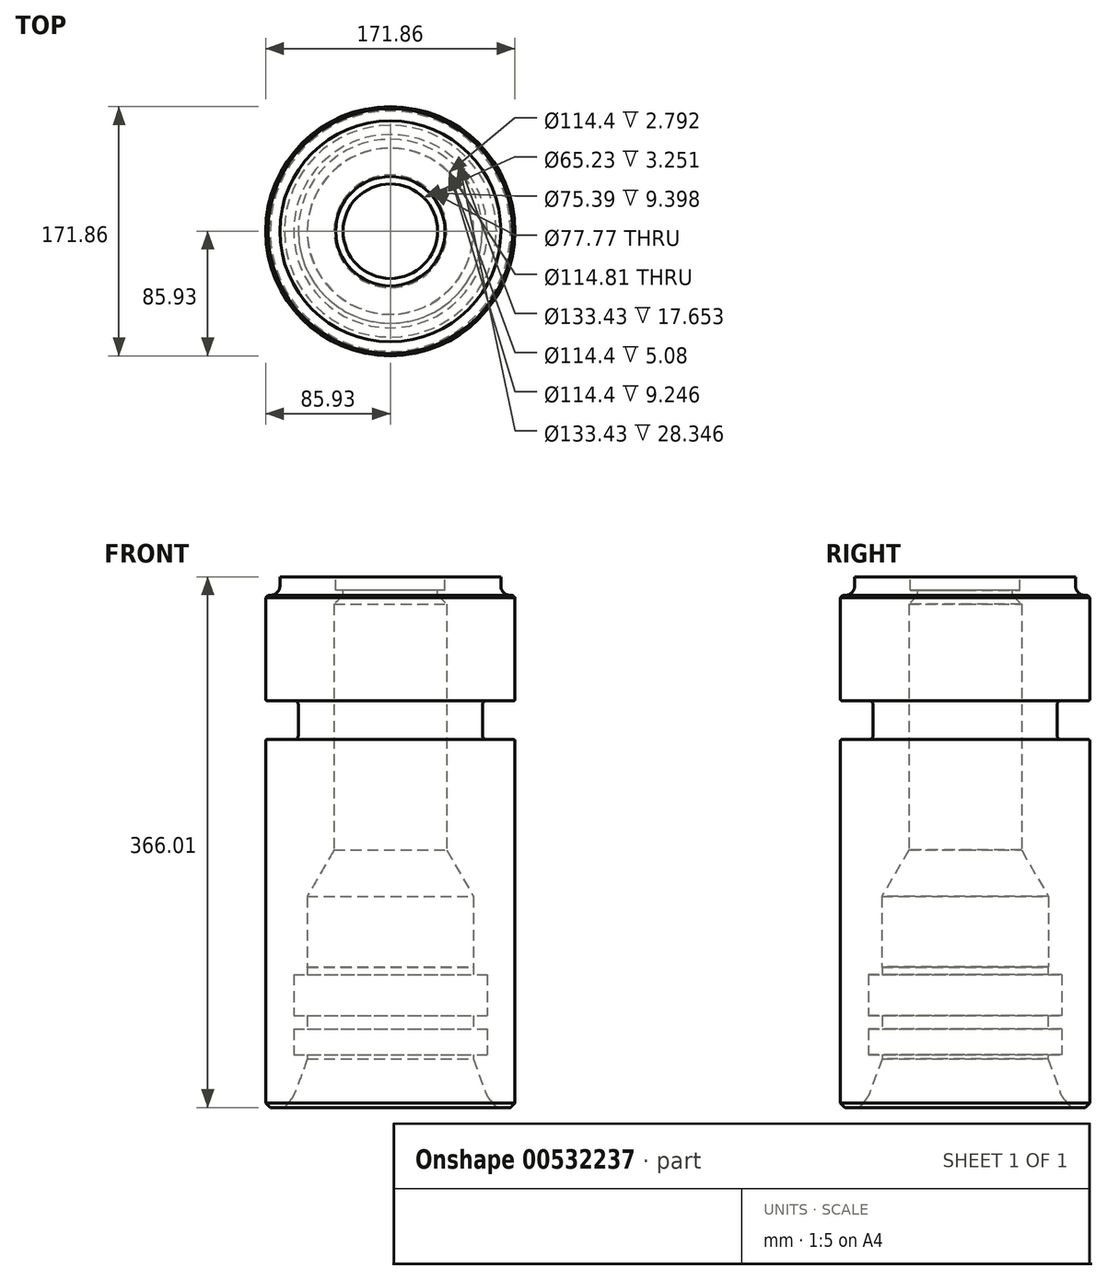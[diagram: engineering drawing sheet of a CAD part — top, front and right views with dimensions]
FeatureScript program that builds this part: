
annotation { "Feature Type Name" : "Feature", "Feature Type Description" : "" }
export const myFeature = defineFeature(function(context is Context, id is Id, definition is map)
    precondition{}
    {
        {
            var Q0;
            Q0=qCreatedBy(makeId("Front.planeOp"),FACE);
            var sketch = newSketch(context, id + "F0", { "sketchPlane" : qUnion([Q0])});
            skLineSegment(sketch, "E0", {"start": v(0, 0) * mm, "end": v(76.2, 0) * mm});
            skLineSegment(sketch, "E1", {"start": v(85.93, -12.7) * mm, "end": v(85.93, -85.34) * mm});
            skLineSegment(sketch, "E2", {"start": v(85.93, -366.01) * mm, "end": v(0, -366.01) * mm});
            skLineSegment(sketch, "E3", {"start": v(0, -366.01) * mm, "end": v(0, 0) * mm});
            skLineSegment(sketch, "E4", {"start": v(85.93, -112.27) * mm, "end": v(63.46, -112.27) * mm});
            skLineSegment(sketch, "E5", {"start": v(63.46, -112.27) * mm, "end": v(63.46, -85.34) * mm});
            skLineSegment(sketch, "E6", {"start": v(63.46, -85.34) * mm, "end": v(85.93, -85.34) * mm});
            skLineSegment(sketch, "E7.trimOffspring", {"start": v(85.93, -112.27) * mm, "end": v(85.93, -366.01) * mm});
            skLineSegment(sketch, "E8", {"start": v(85.93, -12.7) * mm, "end": v(76.2, -12.7) * mm});
            skLineSegment(sketch, "E9", {"start": v(76.2, -12.7) * mm, "end": v(76.2, 0) * mm});
            skPoint(sketch, "E10.orphan", {"position": v(85.93, 0) * mm});
            skSolve(sketch);
        }
        {
            var Q0;
            Q0=makeQuery(id+"F0.imprint","IMPRINT",FACE,{"disambiguationData":[TD([[makeQuery(id+"F0.imprint","IMPRINT",EDGE,{"derivedFrom":sQuery(id+"F0.wireOp",EDGE,"E0")}),-1.0]])]});
            var Q1;
            Q1=sQuery(id+"F0.wireOp",EDGE,"E3");
            revolve(context, id + "F1", {"entities" : qUnion([Q0]), "axis" : qUnion([Q1]), "revolveType" : RevolveType.FULL});
        }
        {
            var Q0;
            Q0=makeQuery(id+"F1.opRevolve","SWEPT_EDGE",EDGE,{"disambiguationData":[OSD([sQuery(id+"F0.wireOp",EDGE,"E8"),sQuery(id+"F0.wireOp",EDGE,"E9")])]});
            fillet(context, id + "F2", {"entities" : qUnion([Q0]), "radius" : 6.35 * mm, "tangentPropagation" : true, "allowEdgeOverflow" : false});
        }
        {
            var Q0;
            Q0=makeQuery(id+"F1.opRevolve","SWEPT_EDGE",EDGE,{"disambiguationData":[OSD([sQuery(id+"F0.wireOp",EDGE,"E1"),sQuery(id+"F0.wireOp",EDGE,"E8")])]});
            chamfer(context, id + "F3", {"entities" : qUnion([Q0]), "chamferType" : ChamferType.OFFSET_ANGLE, "width" : 1.52 * mm, "oppositeDirection" : false, "angle" : 45 * degree, "tangentPropagation" : true});
        }
        {
            var Q0;
            Q0=makeQuery(id+"F1.opRevolve","SWEPT_FACE",FACE,{"disambiguationData":[OSD([sQuery(id+"F0.wireOp",EDGE,"E0")])]});
            var sketch = newSketch(context, id + "F4", { "sketchPlane" : qUnion([Q0])});
            skCircle(sketch, "E11", {"center": v(0, 0) * mm, "radius": 32.61 * mm});
            skSolve(sketch);
        }
        {
            var Q0;
            Q0=makeQuery(id+"F4.imprint","IMPRINT",FACE,{"disambiguationData":[TD([[makeQuery(id+"F4.imprint","IMPRINT",EDGE,{"derivedFrom":sQuery(id+"F4.wireOp",EDGE,"E11")}),1.0]])]});
            var Q1;
            Q1=sQuery(id+"F4.wireOp",EDGE,"E11");
            extrude(context, id + "F5", {"entities" : qUnion([Q0]), "operationType" : NewBodyOperationType.REMOVE, "surfaceEntities" : qUnion([Q1]), "endBound" : BoundingType.THROUGH_ALL, "oppositeDirection" : true, "depth" : 25.4 * mm, "offsetDistance" : 25.4 * mm});
        }
        {
            var Q0;
            Q0=makeQuery(id+"F1.opRevolve","SWEPT_FACE",FACE,{"disambiguationData":[OSD([sQuery(id+"F0.wireOp",EDGE,"E2")])]});
            var sketch = newSketch(context, id + "F6", { "sketchPlane" : qUnion([Q0])});
            skCircle(sketch, "E12", {"center": v(0, 0) * mm, "radius": 57.2 * mm});
            skSolve(sketch);
        }
        {
            var Q0;
            Q0=makeQuery(id+"F6.imprint","IMPRINT",FACE,{"disambiguationData":[TD([[makeQuery(id+"F6.imprint","IMPRINT",EDGE,{"derivedFrom":sQuery(id+"F6.wireOp",EDGE,"E12")}),1.0]])]});
            var Q1;
            Q1=sQuery(id+"F6.wireOp",EDGE,"E12");
            extrude(context, id + "F7", {"entities" : qUnion([Q0]), "operationType" : NewBodyOperationType.REMOVE, "surfaceEntities" : qUnion([Q1]), "oppositeDirection" : true, "depth" : 145.54 * mm, "offsetDistance" : 25.4 * mm});
        }
        {
            var Q0;
            Q0=makeQuery(id+"F1.opRevolve","SWEPT_FACE",FACE,{"disambiguationData":[OSD([sQuery(id+"F0.wireOp",EDGE,"E0")])]});
            var sketch = newSketch(context, id + "F8", { "sketchPlane" : qUnion([Q0])});
            skCircle(sketch, "E13", {"center": v(0, 0) * mm, "radius": 37.7 * mm});
            skSolve(sketch);
        }
        {
            var Q0;
            Q0=makeQuery(id+"F8.imprint","IMPRINT",FACE,{"disambiguationData":[TD([[makeQuery(id+"F8.imprint","IMPRINT",EDGE,{"derivedFrom":sQuery(id+"F8.wireOp",EDGE,"E13")}),1.0]])]});
            var Q1;
            Q1=sQuery(id+"F8.wireOp",EDGE,"E13");
            extrude(context, id + "F9", {"entities" : qUnion([Q0]), "operationType" : NewBodyOperationType.REMOVE, "surfaceEntities" : qUnion([Q1]), "oppositeDirection" : true, "depth" : 9.4 * mm, "offsetDistance" : 25.4 * mm});
        }
        {
            var Q0;
            Q0=makeQuery(id+"F1.opRevolve","SWEPT_FACE",FACE,{"disambiguationData":[OSD([sQuery(id+"F0.wireOp",EDGE,"E2")])]});
            var sketch = newSketch(context, id + "F10", { "sketchPlane" : qUnion([Q0])});
            skCircle(sketch, "E14", {"center": v(0, 0) * mm, "radius": 38.89 * mm});
            skSolve(sketch);
        }
        {
            var Q0;
            Q0=makeQuery(id+"F10.imprint","IMPRINT",FACE,{"disambiguationData":[TD([[makeQuery(id+"F10.imprint","IMPRINT",EDGE,{"derivedFrom":sQuery(id+"F10.wireOp",EDGE,"E14")}),1.0]])]});
            var Q1;
            Q1=sQuery(id+"F10.wireOp",EDGE,"E14");
            extrude(context, id + "F11", {"entities" : qUnion([Q0]), "operationType" : NewBodyOperationType.REMOVE, "surfaceEntities" : qUnion([Q1]), "oppositeDirection" : true, "depth" : 347.1 * mm, "offsetDistance" : 25.4 * mm});
        }
        {
            var Q0;
            Q0=qCreatedBy(makeId("Front.planeOp"),FACE);
            var sketch = newSketch(context, id + "F12", { "sketchPlane" : qUnion([Q0])});
            skLineSegment(sketch, "E15", {"start": v(0, 0) * mm, "end": v(0, -453.27) * mm, "construction": true});
            skLineSegment(sketch, "E16", {"start": v(-66.71, -441.11) * mm, "end": v(-66.71, -208.96) * mm, "construction": true});
            skLineSegment(sketch, "E17", {"start": v(-73.02, -439) * mm, "end": v(-73.03, -203.14) * mm, "construction": true});
            skLineSegment(sketch, "E18", {"start": v(-57.2, -377.44) * mm, "end": v(-57.2, -233.84) * mm, "construction": true});
            skLineSegment(sketch, "E19", {"start": v(97.13, -366.01) * mm, "end": v(-142.82, -366.01) * mm, "construction": true});
            skLineSegment(sketch, "E20", {"start": v(-73.02, -366.01) * mm, "end": v(-66.71, -358.5) * mm});
            skLineSegment(sketch, "E21", {"start": v(-66.71, -358.5) * mm, "end": v(-57.2, -332.36) * mm});
            skLineSegment(sketch, "E22", {"start": v(-57.2, -332.36) * mm, "end": v(-57.2, -366.01) * mm});
            skLineSegment(sketch, "E23", {"start": v(-57.2, -366.01) * mm, "end": v(-73.02, -366.01) * mm});
            skSolve(sketch);
        }
        {
            var Q0;
            Q0 = qSketchRegion(id + "F12", true);
            var Q1;
            Q1=sQuery(id+"F12.wireOp",EDGE,"E15");
            revolve(context, id + "F13", {"operationType" : NewBodyOperationType.REMOVE, "entities" : qUnion([Q0]), "axis" : qUnion([Q1]), "revolveType" : RevolveType.FULL, "oppositeDirection" : true});
        }
        {
            var Q0;
            Q0=qCreatedBy(makeId("Front.planeOp"),FACE);
            var sketch = newSketch(context, id + "F14", { "sketchPlane" : qUnion([Q0])});
            skLineSegment(sketch, "E24", {"start": v(0, 19.06) * mm, "end": v(0, -574.27) * mm, "construction": true});
            skLineSegment(sketch, "E25", {"start": v(0, -329.57) * mm, "end": v(-66.71, -329.57) * mm});
            skLineSegment(sketch, "E26", {"start": v(-66.71, -329.57) * mm, "end": v(-66.71, -311.91) * mm});
            skLineSegment(sketch, "E27", {"start": v(-66.71, -311.91) * mm, "end": v(-57.2, -311.91) * mm});
            skLineSegment(sketch, "E28", {"start": v(-57.2, -311.91) * mm, "end": v(-57.2, -302.67) * mm});
            skLineSegment(sketch, "E29", {"start": v(-57.2, -302.67) * mm, "end": v(-66.71, -302.67) * mm});
            skLineSegment(sketch, "E30", {"start": v(-66.71, -302.67) * mm, "end": v(-66.71, -274.32) * mm});
            skLineSegment(sketch, "E31", {"start": v(-66.71, -274.32) * mm, "end": v(-57.2, -274.32) * mm});
            skLineSegment(sketch, "E32", {"start": v(-57.2, -274.32) * mm, "end": v(-57.2, -269.24) * mm});
            skLineSegment(sketch, "E33", {"start": v(-57.2, -269.24) * mm, "end": v(-57.4, -269.04) * mm});
            skLineSegment(sketch, "E34", {"start": v(-57.4, -269.04) * mm, "end": v(-57.4, -220.47) * mm});
            skLineSegment(sketch, "E35", {"start": v(0, -329.57) * mm, "end": v(0, -220.47) * mm});
            skLineSegment(sketch, "E36", {"start": v(-57.4, -220.47) * mm, "end": v(-38.89, -188.4) * mm});
            skLineSegment(sketch, "E37", {"start": v(-38.89, -188.4) * mm, "end": v(-38.89, -162.81) * mm});
            skLineSegment(sketch, "E38", {"start": v(-38.89, -162.81) * mm, "end": v(0, -162.81) * mm});
            skLineSegment(sketch, "E39", {"start": v(0, -329.57) * mm, "end": v(0, -162.81) * mm});
            skSolve(sketch);
        }
        {
            var Q0;
            {var subQ0=sQuery(id+"F14.wireOp",EDGE,"E25");Q0=makeQuery(id+"F14.imprint","IMPRINT",FACE,{"disambiguationData":[TD([[makeQuery(id+"F14.imprint","IMPRINT",EDGE,{"derivedFrom":subQ0}),-1.0]])]});}
            var Q1;
            Q1=sQuery(id+"F14.wireOp",EDGE,"E24");
            revolve(context, id + "F15", {"operationType" : NewBodyOperationType.REMOVE, "entities" : qUnion([Q0]), "axis" : qUnion([Q1]), "revolveType" : RevolveType.FULL, "oppositeDirection" : true});
        }
        {
            var Q0;
            Q0=qCreatedBy(makeId("Front.planeOp"),FACE);
            var sketch = newSketch(context, id + "F16", { "sketchPlane" : qUnion([Q0])});
            skLineSegment(sketch, "E40", {"start": v(0, 21) * mm, "end": v(0, -38.61) * mm, "construction": true});
            skLineSegment(sketch, "E41", {"start": v(38.89, -18.92) * mm, "end": v(32.61, -12.65) * mm});
            skLineSegment(sketch, "E42", {"start": v(32.61, -12.65) * mm, "end": v(0, -12.65) * mm});
            skLineSegment(sketch, "E43", {"start": v(0, -12.65) * mm, "end": v(0, -18.92) * mm});
            skLineSegment(sketch, "E44", {"start": v(0, -18.92) * mm, "end": v(38.89, -18.92) * mm});
            skSolve(sketch);
        }
        {
            var Q0;
            Q0 = qSketchRegion(id + "F16", true);
            var Q1;
            Q1=sQuery(id+"F16.wireOp",EDGE,"E40");
            revolve(context, id + "F17", {"operationType" : NewBodyOperationType.REMOVE, "entities" : qUnion([Q0]), "axis" : qUnion([Q1]), "revolveType" : RevolveType.FULL, "oppositeDirection" : true});
        }
        {
            var Q0;
            Q0=makeQuery(id+"F1.opRevolve","SWEPT_EDGE",EDGE,{"disambiguationData":[OSD([sQuery(id+"F0.wireOp",EDGE,"E4"),sQuery(id+"F0.wireOp",EDGE,"E5")])]});
            var Q1;
            Q1=makeQuery(id+"F1.opRevolve","SWEPT_EDGE",EDGE,{"disambiguationData":[OSD([sQuery(id+"F0.wireOp",EDGE,"E5"),sQuery(id+"F0.wireOp",EDGE,"E6")])]});
            fillet(context, id + "F18", {"entities" : qUnion([Q0, Q1]), "radius" : 3.05 * mm, "tangentPropagation" : true, "allowEdgeOverflow" : false});
        }
        {
            var Q0;
            Q0=makeQuery(id+"F1.opRevolve","SWEPT_EDGE",EDGE,{"disambiguationData":[OSD([sQuery(id+"F0.wireOp",EDGE,"E2"),sQuery(id+"F0.wireOp",EDGE,"E7.trimOffspring")])]});
            chamfer(context, id + "F19", {"entities" : qUnion([Q0]), "chamferType" : ChamferType.OFFSET_ANGLE, "width" : 3.05 * mm, "oppositeDirection" : false, "angle" : 45 * degree, "tangentPropagation" : true});
        }
        {
            var Q0;
            Q0=makeQuery(id+"F13.boolean.opBoolean","COPY",EDGE,{"derivedFrom":makeQuery(id+"F13.opRevolve","SWEPT_EDGE",EDGE,{"disambiguationData":[OSD([sQuery(id+"F12.wireOp",EDGE,"E20"),sQuery(id+"F12.wireOp",EDGE,"E21")])]})});
            fillet(context, id + "F20", {"entities" : qUnion([Q0]), "radius" : 19.05 * mm, "tangentPropagation" : true, "allowEdgeOverflow" : false});
        }
        {
            var Q0;
            Q0=makeQuery(id+"F1.opRevolve","SWEPT_EDGE",EDGE,{"disambiguationData":[OSD([sQuery(id+"F0.wireOp",EDGE,"E4"),sQuery(id+"F0.wireOp",EDGE,"E7.trimOffspring")])]});
            var Q1;
            Q1=makeQuery(id+"F1.opRevolve","SWEPT_EDGE",EDGE,{"disambiguationData":[OSD([sQuery(id+"F0.wireOp",EDGE,"E1"),sQuery(id+"F0.wireOp",EDGE,"E6")])]});
            fillet(context, id + "F21", {"entities" : qUnion([Q0, Q1]), "radius" : 0.76 * mm, "tangentPropagation" : true, "allowEdgeOverflow" : false});
        }
    });
